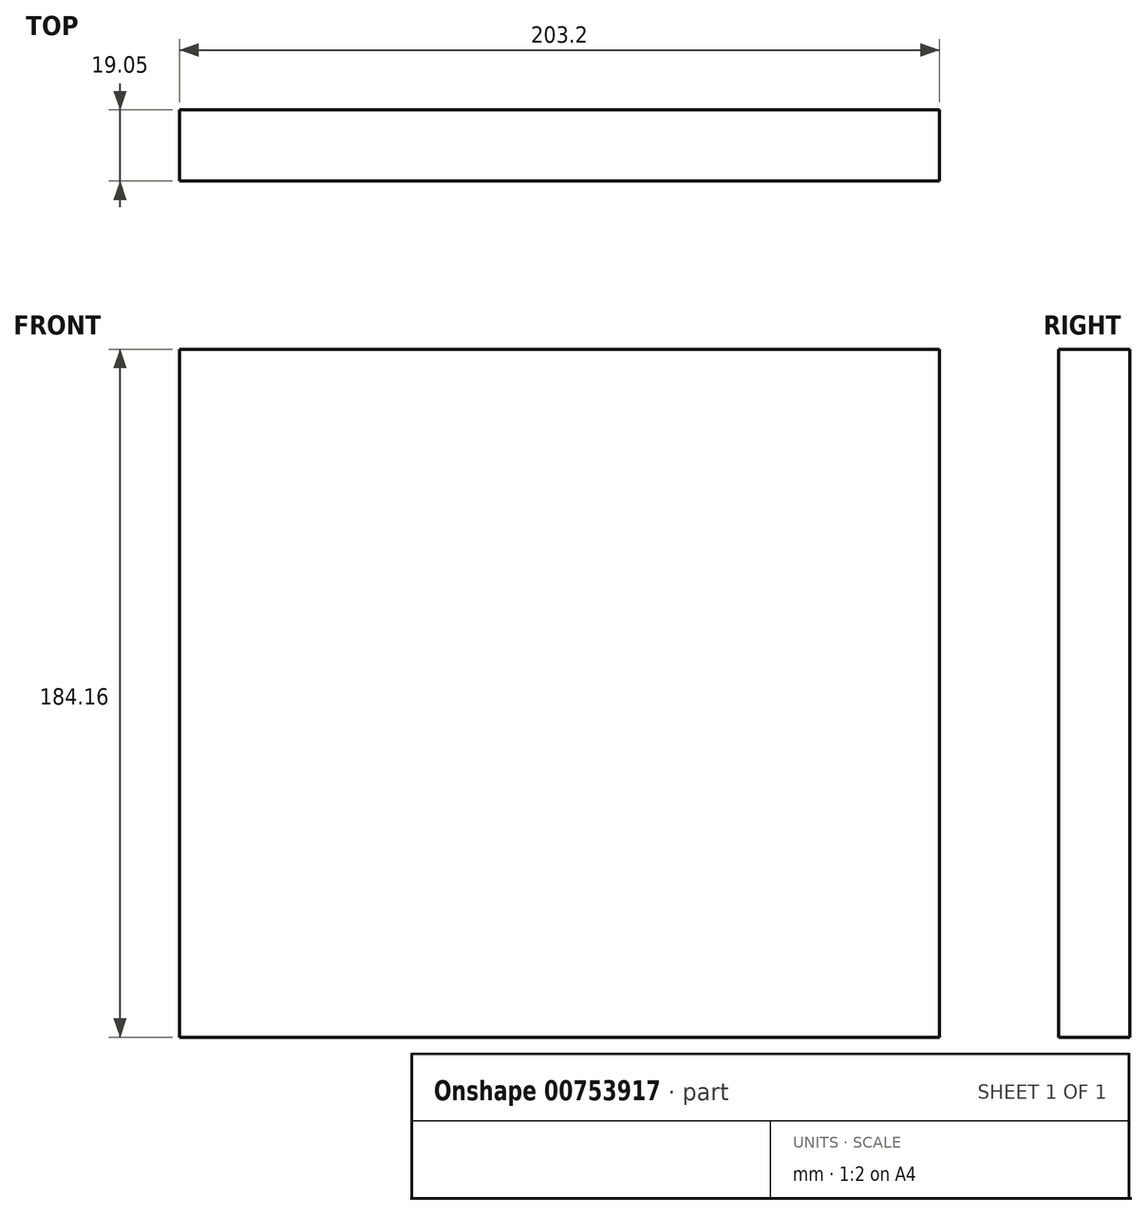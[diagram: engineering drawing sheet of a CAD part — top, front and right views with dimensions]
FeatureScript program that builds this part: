
annotation { "Feature Type Name" : "Feature", "Feature Type Description" : "" }
export const myFeature = defineFeature(function(context is Context, id is Id, definition is map)
    precondition{}
    {
        {
            var Q0;
            Q0=qCreatedBy(makeId("Front.planeOp"),FACE);
            var sketch = newSketch(context, id + "F0", { "sketchPlane" : qUnion([Q0])});
            skLineSegment(sketch, "E0.bottom", {"start": v(101.6, -92.07) * mm, "end": v(-101.6, -92.07) * mm});
            skLineSegment(sketch, "E0.top", {"start": v(101.6, 92.08) * mm, "end": v(-101.6, 92.07) * mm});
            skLineSegment(sketch, "E0.left", {"start": v(101.6, -92.07) * mm, "end": v(101.6, 92.08) * mm});
            skLineSegment(sketch, "E0.right", {"start": v(-101.6, -92.07) * mm, "end": v(-101.6, 92.08) * mm});
            skPoint(sketch, "E0.middle", {"position": v(0, 0) * mm});
            skSolve(sketch);
        }
        {
            var Q0;
            Q0=makeQuery(id+"F0.imprint","IMPRINT",FACE,{"disambiguationData":[TD([[makeQuery(id+"F0.imprint","IMPRINT",EDGE,{"derivedFrom":sQuery(id+"F0.wireOp",EDGE,"E0.bottom")}),-1.0]])]});
            extrude(context, id + "F1", {"entities" : qUnion([Q0]), "depth" : 19.05 * mm, "offsetDistance" : 25.4 * mm});
        }
    });
